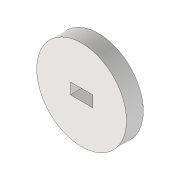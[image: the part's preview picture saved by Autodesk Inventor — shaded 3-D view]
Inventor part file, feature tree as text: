
AUTODESK INVENTOR PART (.ipt)
format: ipt  version: 2020 (Build 240168000, 168)  size: 84,480 bytes
history: native  units: mm
features: extrude x1, sketch x1
ambient origin geometry x8: Origin, YZ Plane, XZ Plane, XY Plane, X Axis, Y Axis, Z Axis, Center Point
bodies: Volumenkörper1 (feature_tree)
feature tree (2):
  extrude  "Extrusion1"  Depth=10.0mm
  sketch  "Skizze1"  dims[d0=20.0mm d1=10.0mm d2=80.0mm d3=15.0mm d4=0.0mm]
